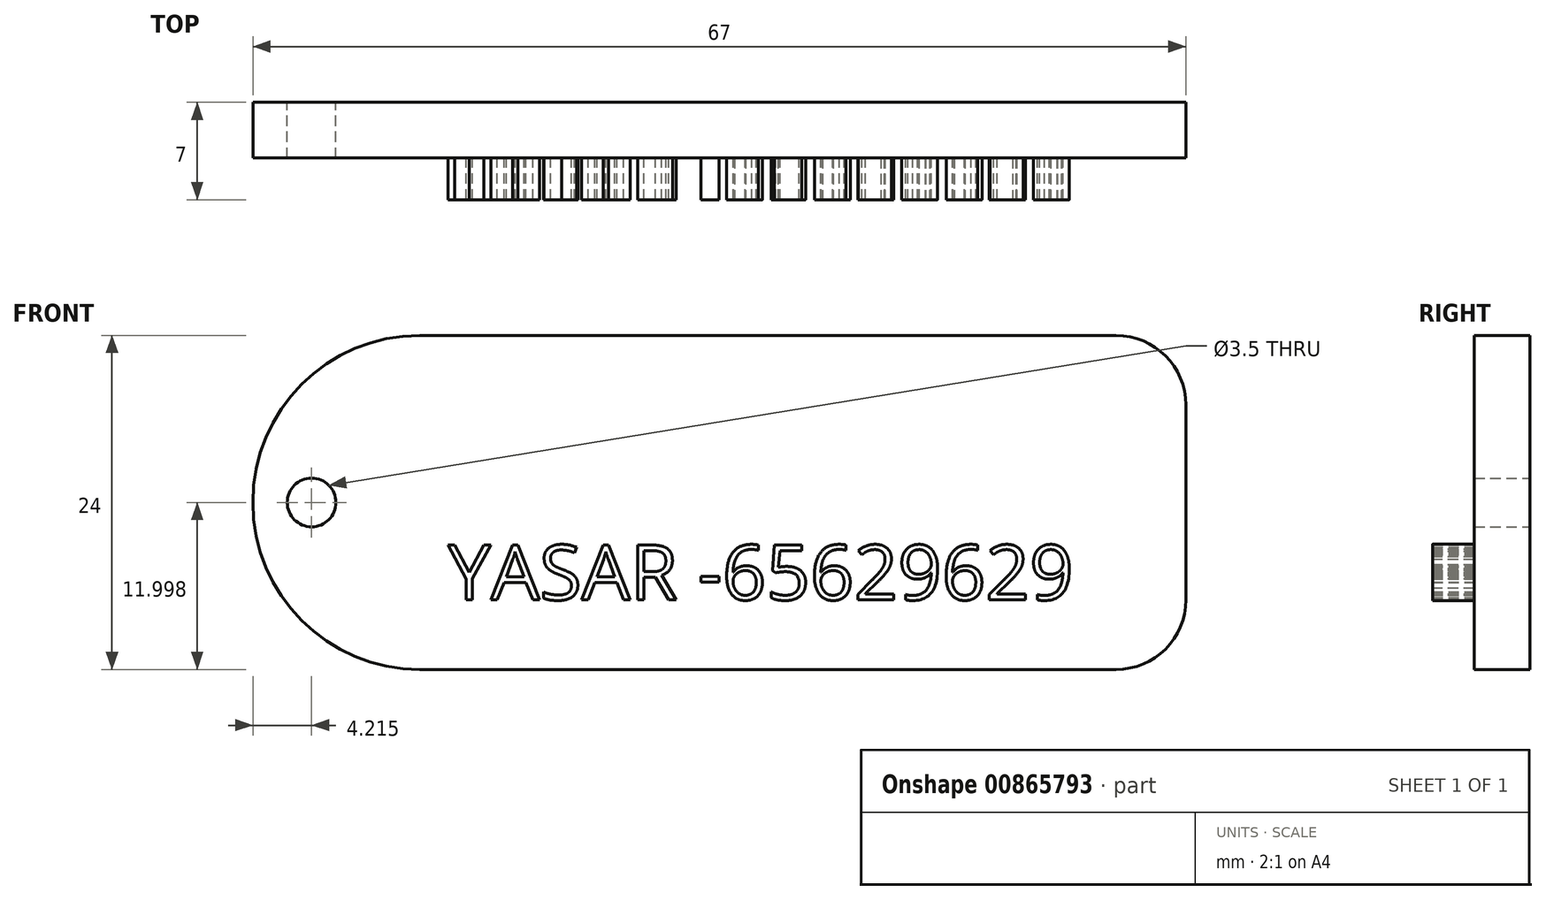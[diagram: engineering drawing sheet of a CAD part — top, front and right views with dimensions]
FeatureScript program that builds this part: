
annotation { "Feature Type Name" : "Feature", "Feature Type Description" : "" }
export const myFeature = defineFeature(function(context is Context, id is Id, definition is map)
    precondition{}
    {
        {
            var Q0;
            Q0=qCreatedBy(makeId("Front.planeOp"),FACE);
            var sketch = newSketch(context, id + "F0", { "sketchPlane" : qUnion([Q0])});
            skLineSegment(sketch, "E0.bottom", {"start": v(-45.87, 26.96) * mm, "end": v(4.13, 26.96) * mm});
            skLineSegment(sketch, "E0.top", {"start": v(-45.87, 2.96) * mm, "end": v(4.13, 2.96) * mm});
            skLineSegment(sketch, "E0.right", {"start": v(9.13, 21.96) * mm, "end": v(9.13, 7.96) * mm});
            skArc(sketch, "E1", {"start": v(-45.87, 26.96) * mm, "mid": v(-57.87, 14.96) * mm, "end": v(-45.87, 2.96) * mm});
            skPoint(sketch, "E2.visualSharp", {"position": v(9.13, 26.96) * mm});
            skArc(sketch, "E2.filletArc", {"start": v(9.13, 21.96) * mm, "mid": v(7.66, 25.5) * mm, "end": v(4.13, 26.96) * mm});
            skPoint(sketch, "E3.visualSharp", {"position": v(9.13, 2.96) * mm});
            skArc(sketch, "E3.filletArc", {"start": v(4.13, 2.96) * mm, "mid": v(7.66, 4.42) * mm, "end": v(9.13, 7.96) * mm});
            skCircle(sketch, "E4", {"center": v(-53.66, 14.96) * mm, "radius": 1.75 * mm});
            skSolve(sketch);
        }
        {
            var Q0;
            Q0=makeQuery(id+"F0.imprint","IMPRINT",FACE,{"disambiguationData":[TD([[makeQuery(id+"F0.imprint","IMPRINT",EDGE,{"derivedFrom":sQuery(id+"F0.wireOp",EDGE,"E0.bottom")}),-1.0]])]});
            extrude(context, id + "F1", {"entities" : qUnion([Q0]), "depth" : 4 * mm, "offsetDistance" : 25 * mm});
        }
        {
            var Q0;
            Q0=makeQuery(id+"F1.opExtrude","CAP_FACE",FACE,{"disambiguationData":[OSD([sQuery(id+"F0.wireOp",EDGE,"E0.bottom"),sQuery(id+"F0.wireOp",EDGE,"E0.top"),sQuery(id+"F0.wireOp",EDGE,"E0.right"),sQuery(id+"F0.wireOp",EDGE,"E1"),sQuery(id+"F0.wireOp",EDGE,"E2.filletArc"),sQuery(id+"F0.wireOp",EDGE,"E3.filletArc"),sQuery(id+"F0.wireOp",EDGE,"E4")])],"isStart":false});
            var sketch = newSketch(context, id + "F2", { "sketchPlane" : qUnion([Q0])});
            skText(sketch, "E5", { "text": "YASAR -65629629", "fontName": "OpenSans-Regular.ttf"});
            const initialGuessF2  = {"E5": [-0.04387, 0.00796, 1, 0, 0.00397]};
            skSetInitialGuess(sketch, initialGuessF2);
            skSolve(sketch);
        }
        {
            var Q0;
            Q0 = qSketchRegion(id + "F2", true);
            extrude(context, id + "F3", {"entities" : qUnion([Q0]), "operationType" : NewBodyOperationType.ADD, "depth" : 3 * mm, "offsetDistance" : 25 * mm});
        }
    });
